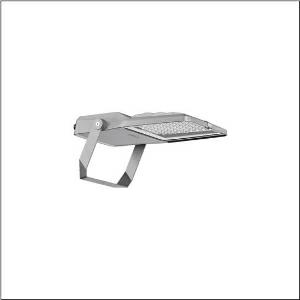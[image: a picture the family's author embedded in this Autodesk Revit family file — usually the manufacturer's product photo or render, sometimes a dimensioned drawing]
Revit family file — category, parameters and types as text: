
# Revit family: floodlight_fl_21_iq_mini___rs12_5xa7771c4b1a_004d
name_source: partatom
category: Lighting Fixtures
units: mm (PartAtom-declared; Revit-internal decimal feet)

## family parameters
Cut with Voids When Loaded = No
Host = Face
Light Source = No
Part Type = Normal
Room Calculation Point = No
Round Connector Dimension = Use Diameter
Shared = No

## types (1)
- --- (1 x LED, 12860 lm, 87.2 W, 4000K)
    Apparent Load = 87 VA
    CIE Flux Codes = 79 92 99 100 100
    Color Rendering = 70
    Color Temperature = 4000K
    Default Elevation = 1800 mm
    Description = Floodlight FL 21 iQ mini, floodlight, primary light control with lens, of PMMA, primary optical cover: protective disc, of toughened safety glass, transparent, light distribution: RS12, light emission: direct distribution, installation type: surface-mounted, LED, High Power LED, rated luminous flux: 12.860lm, luminous efficacy: 148lm/W, light colour: 740, colour temperature: 4000K, control gear: iQ Comfort/DALI, control: Auto-Match, Temp-Guard, Lumen-Switch, Night-Set, Smart-Wire, Light-Fading, Desk-Remote (wireless, voltage-free reading and setting of iQ features in the workshop via application-optimized NFC function/RFID function), optimised constant luminous flux control (CLO 2.0), with terminal, 6-pole, mains connection: 220..240V, AC, 50/60Hz, start of lifetime: 87W, end of service life: 92W, reduction: 40W, luminaire housing, of diecast aluminium, powder-coated, Siteco® metallic grey (DB 702S), corrosivity category C5 mid according to DIN EN ISO 12944, suitable for swimming pools, chlorine-resistant, sealing non-destructively replaceable, mounting bracket, of steel, galvanised, powder-coated, Siteco® metallic grey (DB 702S), protection rating (complete): IP66, insulation class (complete): insulation class II (safety insulation), certification: CE, ENEC, VDE, protection symbol: D, impact resistance: IK08, permissible operating ambient temperature: -40..+40°C, permissible operating ambient temperature for outdoor applications: -40..+50°C, standard: DIN EN 12944, LABS conformity tested according to VDMA 24364:2018-05, packaging unit: 1 piece

Light Distribution: RS12
    Height = 70 mm
    Lamp = 1 x LED
    Lamp Light Flux = 12860 lm
    Lamp Power = 87.2 W
    Lamp count = 1
    Length = 485 mm
    Luminous efficacy = 147 lm/W
    Manufacturer = Siteco
    ModVariant = No
    Model = 5XA7771C4B1A
    Number of Poles = 1
    OnlyDefault = Yes
    Power Factor = 1
    Product Name = Floodlight FL 21 iQ mini | RS12
    Product group = floodlight | pylon annexe
    ProductGroupID = 6200
    Protection Class = Protection class II
    Protection Degree = IP 66
    RLX_Detail_Level = 1
    RLX_Emergency_Light_Flux = 0 lm
    RLX_Emergency_Type = 0
    RLX_Emergency_Type_DB = No
    RlxData = <blob elided: 91125 chars, md5=006d55b8>
    Socket = socket
    Standby Power = 0 W
    System Light Flux = 12860 lm
    System Power = 87 W
    Type Comments = factory setting: luminous flux: 100 % | dim-lin: 254 | 456 mA
    Type Image = l_1006845.jpg
    URL = http://relux.com
    VarID = @adj_167708
    Voltage = 0 V
    Weight = 0.00 kg
    Width = 337 mm

## geometry (parser evidence)
native form markers: Blend x4, Sweep x13
no freeform markers — native parametric forms only
